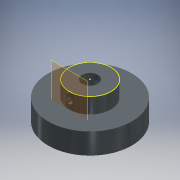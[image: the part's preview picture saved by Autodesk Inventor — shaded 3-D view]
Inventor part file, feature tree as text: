
AUTODESK INVENTOR PART (.ipt)
format: ipt  version: 2020 (Build 240168000, 168)  size: 133,120 bytes
history: native  units: in
note: dims shown in document units (in); Inventor stores cm internally (conversion verified against a paired STEP export)
features: sketch x3, revolve x1, plane x1, hole x1
ambient origin geometry x8: Origin, YZ Plane, XZ Plane, XY Plane, X Axis, Y Axis, Z Axis, Center Point
bodies: Solid1 (feature_tree)
feature tree (6):
  revolve  "Revolution1"  [1 undecoded]
  sketch  "Sketch2"  dims[d2=0.875in d4=0.5in]
  plane  "Work Plane1"
  hole  "Hole1"  [1 undecoded]
  sketch  "Sketch1"  dims[d0=1.0in d1=0.375in]
  sketch  "Sketch3"  dims[d5=2.0in d6=90.0deg d7=0.1875in d8=0.152in d9=0.4629in d10=0.375in d11=0.25in d12=0.5635in d13=1.0in d14=0.8108in]
note: 2 required parameter values undecoded (feature->parameter linkage not recoverable at this tier; creation-order binding heuristic only, values carry confidence <= 0.55)